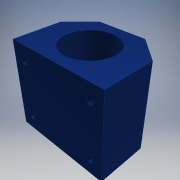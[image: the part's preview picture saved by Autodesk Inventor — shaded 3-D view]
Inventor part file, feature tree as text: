
AUTODESK INVENTOR PART (.ipt)
format: ipt  version: 2018 (Build 220112000, 112)  size: 154,112 bytes
history: native  units: mm
features: sketch x4, hole x3, other x1, extrude x1
ambient origin geometry x8: Origin, YZ Plane, XZ Plane, XY Plane, X Axis, Y Axis, Z Axis, Center Point
bodies: Body1 (feature_tree)
feature tree (9):
  other  "Sólido1"
  extrude  "Extrusión1"  Depth=40.0mm
  hole  "Agujero1"  [1 undecoded]
  hole  "Agujero2"  [1 undecoded]
  hole  "Agujero3"  [1 undecoded]
  sketch  "Boceto2"  dims[d0=20.0mm d1=40.0mm]
  sketch  "Boceto3"  dims[d2=10.0mm d3=10.0mm]
  sketch  "Boceto4"  dims[d4=10.0mm d5=35.0mm d6=0.0mm]
  sketch  "Boceto6"  dims[d7=20.0mm d8=15.0mm d9=21.0mm d10=6.0mm d11=4.0mm d12=2.0mm d13=90.0deg d14=35.0mm d15=20.594885mm d16=23.0mm d17=5.0mm d18=10.0mm d19=5.0mm d20=30.0mm d21=3.0mm d22=6.0mm d23=4.0mm d24=2.0mm d25=90.0deg d26=35.0mm d27=20.594885mm d30=17.5mm d31=35.0mm d32=17.5mm d33=30.0mm d34=23.0mm d35=7.0mm d36=6.0mm d37=4.0mm d38=2.0mm d39=90.0deg d40=10.0mm d41=0.0mm]
note: 3 required parameter values undecoded (feature->parameter linkage not recoverable at this tier; creation-order binding heuristic only, values carry confidence <= 0.55)
